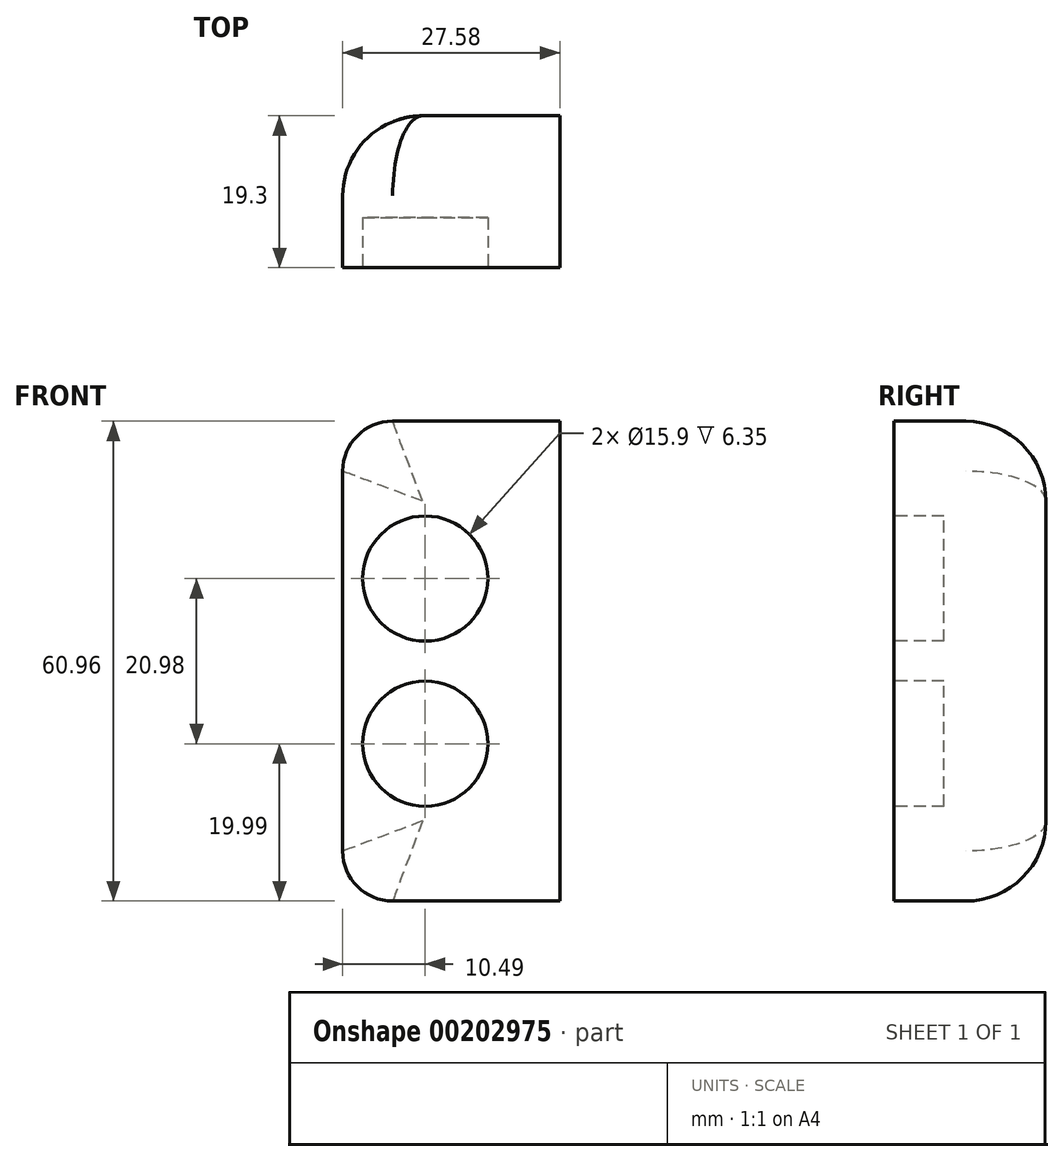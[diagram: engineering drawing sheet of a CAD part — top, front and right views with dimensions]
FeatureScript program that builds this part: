
annotation { "Feature Type Name" : "Feature", "Feature Type Description" : "" }
export const myFeature = defineFeature(function(context is Context, id is Id, definition is map)
    precondition{}
    {
        {
            var Q0;
            Q0=qCreatedBy(makeId("Front.planeOp"),FACE);
            var sketch = newSketch(context, id + "F0", { "sketchPlane" : qUnion([Q0])});
            skLineSegment(sketch, "E0.bottom", {"start": v(0, 0) * mm, "end": v(-20.98, 0) * mm});
            skLineSegment(sketch, "E0.top", {"start": v(0, 30.48) * mm, "end": v(-14.63, 30.48) * mm});
            skLineSegment(sketch, "E0.left", {"start": v(0, 0) * mm, "end": v(0, 30.48) * mm});
            skLineSegment(sketch, "E0.right", {"start": v(-20.98, 0) * mm, "end": v(-20.98, 24.13) * mm});
            skLineSegment(sketch, "E1.MirrorCS", {"start": v(0, 0) * mm, "end": v(0, -30.48) * mm});
            skLineSegment(sketch, "E2.MirrorCS", {"start": v(-20.98, 0) * mm, "end": v(-20.98, -24.13) * mm});
            skLineSegment(sketch, "E3.MirrorCS", {"start": v(0, -30.48) * mm, "end": v(-14.63, -30.48) * mm});
            skPoint(sketch, "E4.visualSharp", {"position": v(-20.98, 30.48) * mm});
            skArc(sketch, "E4.filletArc", {"start": v(-14.63, 30.48) * mm, "mid": v(-19.12, 28.62) * mm, "end": v(-20.98, 24.13) * mm});
            skPoint(sketch, "E5.visualSharp", {"position": v(-20.98, -30.48) * mm});
            skArc(sketch, "E5.filletArc", {"start": v(-20.98, -24.13) * mm, "mid": v(-19.12, -28.62) * mm, "end": v(-14.63, -30.48) * mm});
            skSolve(sketch);
        }
        {
            var Q0;
            Q0=makeQuery(id+"F0.imprint","IMPRINT",FACE,{"disambiguationData":[TD([[makeQuery(id+"F0.imprint","IMPRINT",EDGE,{"derivedFrom":sQuery(id+"F0.wireOp",EDGE,"E0.bottom")}),-1.0]])]});
            var Q1;
            Q1=makeQuery(id+"F0.imprint","IMPRINT",FACE,{"disambiguationData":[TD([[makeQuery(id+"F0.imprint","IMPRINT",EDGE,{"derivedFrom":sQuery(id+"F0.wireOp",EDGE,"E0.bottom")}),1.0]])]});
            extrude(context, id + "F1", {"entities" : qUnion([Q0, Q1]), "depth" : 19.3 * mm});
        }
        {
            var Q0;
            Q0=makeQuery(id+"F1.opExtrude","CAP_FACE",FACE,{"disambiguationData":[OSD([sQuery(id+"F0.wireOp",EDGE,"E0.top"),sQuery(id+"F0.wireOp",EDGE,"E0.left"),sQuery(id+"F0.wireOp",EDGE,"E0.right"),sQuery(id+"F0.wireOp",EDGE,"E1.MirrorCS"),sQuery(id+"F0.wireOp",EDGE,"E2.MirrorCS"),sQuery(id+"F0.wireOp",EDGE,"E3.MirrorCS"),sQuery(id+"F0.wireOp",EDGE,"E4.filletArc"),sQuery(id+"F0.wireOp",EDGE,"E5.filletArc")])],"isStart":false});
            var sketch = newSketch(context, id + "F2", { "sketchPlane" : qUnion([Q0])});
            skCircle(sketch, "E6", {"center": v(-10.5, 10.5) * mm, "radius": 7.95 * mm});
            skCircle(sketch, "E7", {"center": v(-10.5, -10.5) * mm, "radius": 7.95 * mm});
            skSolve(sketch);
        }
        {
            var Q0;
            Q0=qSketchRegion(id+"F2",true);
            extrude(context, id + "F3", {"entities" : qUnion([Q0]), "operationType" : NewBodyOperationType.REMOVE, "oppositeDirection" : true, "depth" : 6.35 * mm});
        }
        {
            var Q0;
            Q0=makeQuery(id+"F1.opExtrude","CAP_EDGE",EDGE,{"disambiguationData":[OSD([sQuery(id+"F0.wireOp",EDGE,"E0.right"),sQuery(id+"F0.wireOp",EDGE,"E2.MirrorCS")])],"isStart":true});
            fillet(context, id + "F4", {"entities" : qUnion([Q0]), "radius" : 10.16 * mm, "tangentPropagation" : true, "allowEdgeOverflow" : false});
        }
        {
            var Q0;
            Q0=makeQuery(id+"F1.opExtrude","SWEPT_FACE",FACE,{"disambiguationData":[OSD([sQuery(id+"F0.wireOp",EDGE,"E0.left"),sQuery(id+"F0.wireOp",EDGE,"E1.MirrorCS")])]});
            extrude(context, id + "F5", {"entities" : qUnion([Q0]), "operationType" : NewBodyOperationType.ADD, "depth" : 6.6 * mm});
        }
    });
